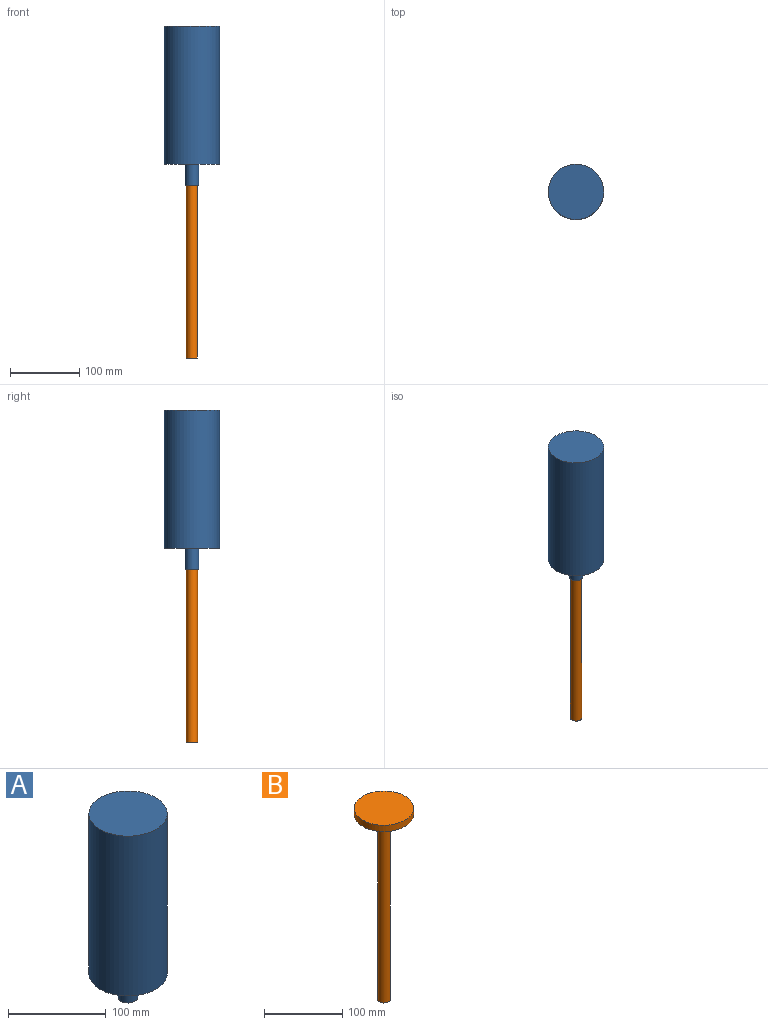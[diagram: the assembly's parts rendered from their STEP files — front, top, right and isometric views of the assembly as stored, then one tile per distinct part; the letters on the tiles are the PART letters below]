
ASSEMBLY  parts=2 mates=1
PART A: 9 faces, bbox 80x80x230 mm
  f0: plane 76x76mm, normal (0,0,-1), area 4536.5mm2, adj f1
  f1: cylinder r=38mm len=196mm, axis (0,0,1), area 46797.2mm2, adj f0,f2
  f2: plane 76x76mm, normal (0,0,1), area 4335.4mm2, adj f1,f3
  f3: cylinder r=8mm len=32mm, axis (0,0,1), area 1608.5mm2, adj f2,f4
  f4: plane 20x20mm, normal (0,0,-1), area 113.1mm2, adj f3,f5
  f5: cylinder r=10mm len=30mm, axis (0,0,1), area 1885mm2, adj f4,f6
  f6: plane 80x80mm, normal (0,0,-1), area 4712.4mm2, adj f5,f7
  f7: cylinder r=40mm len=200mm, axis (0,0,1), area 50265.5mm2, adj f6,f8
  f8: plane 80x80mm, normal (0,0,1), area 5026.5mm2, adj f7
PART B: 5 faces, bbox 76x76x300 mm
  f0: plane 76x76mm, normal (0,0,1), area 4536.5mm2, adj f4
  f1: plane 16x16mm, normal (0,0,-1), area 201.1mm2, adj f2
  f2: cylinder r=8mm len=290mm, axis (0,0,-1), area 14577mm2, adj f1,f3
  f3: plane 76x76mm, normal (0,0,-1), area 4335.4mm2, adj f2,f4
  f4: cylinder r=38mm len=76mm, axis (0,0,-1), area 2387.6mm2, adj f0,f3
PLACE A t=(-19.29,0,153.57)mm fixed
PLACE B t=(0,0,-80)mm
MATE slider A.f1 <-> B.f2  axis (0,0,1) through (0,0,187.38)mm
